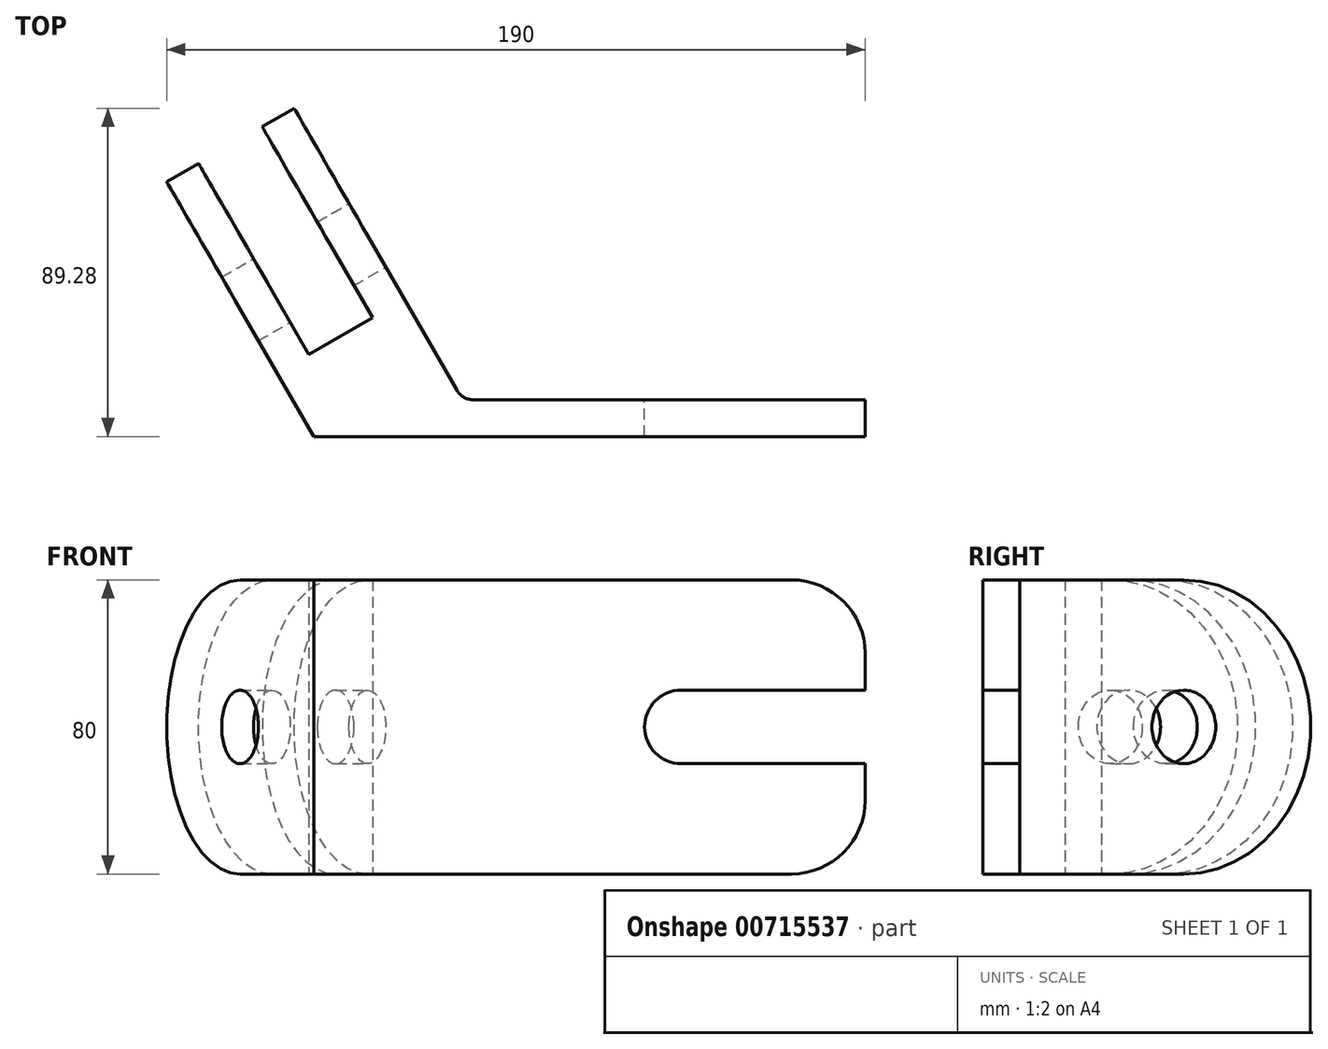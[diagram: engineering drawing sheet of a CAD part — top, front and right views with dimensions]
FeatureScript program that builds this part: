
annotation { "Feature Type Name" : "Feature", "Feature Type Description" : "" }
export const myFeature = defineFeature(function(context is Context, id is Id, definition is map)
    precondition{}
    {
        {
            var Q0;
            Q0=qCreatedBy(makeId("Top.planeOp"),FACE);
            var sketch = newSketch(context, id + "F0", { "sketchPlane" : qUnion([Q0])});
            skPoint(sketch, "E0.middle", {"position": v(0, 0) * mm});
            skLineSegment(sketch, "E1", {"start": v(0, 0) * mm, "end": v(150, 0) * mm});
            skLineSegment(sketch, "E2", {"start": v(150, 0) * mm, "end": v(150, 10) * mm});
            skLineSegment(sketch, "E3", {"start": v(0, 0) * mm, "end": v(-40, 69.28) * mm});
            skLineSegment(sketch, "E4", {"start": v(-40, 69.28) * mm, "end": v(-5.36, 89.28) * mm});
            skLineSegment(sketch, "E5", {"start": v(-5.36, 89.28) * mm, "end": v(40.41, 10) * mm});
            skLineSegment(sketch, "E6", {"start": v(150, 10) * mm, "end": v(40.41, 10) * mm});
            skLineSegment(sketch, "E7", {"start": v(-40, 69.28) * mm, "end": v(-31.34, 74.28) * mm});
            skLineSegment(sketch, "E8", {"start": v(-31.34, 74.28) * mm, "end": v(-1.34, 22.32) * mm});
            skLineSegment(sketch, "E9", {"start": v(-1.34, 22.32) * mm, "end": v(15.98, 32.32) * mm});
            skLineSegment(sketch, "E10", {"start": v(15.98, 32.32) * mm, "end": v(-14.02, 84.28) * mm});
            skSolve(sketch);
        }
        {
            var Q0;
            Q0=makeQuery(id+"F0.imprint","IMPRINT",FACE,{"disambiguationData":[TD([[makeQuery(id+"F0.imprint","IMPRINT",EDGE,{"derivedFrom":sQuery(id+"F0.wireOp",EDGE,"E1")}),1.0]])]});
            extrude(context, id + "F1", {"entities" : qUnion([Q0]), "depth" : 80 * mm, "offsetDistance" : 25 * mm});
        }
        {
            var Q0;
            Q0=makeQuery(id+"F1.opExtrude","SWEPT_FACE",FACE,{"disambiguationData":[OSD([sQuery(id+"F0.wireOp",EDGE,"E6")])]});
            var sketch = newSketch(context, id + "F2", { "sketchPlane" : qUnion([Q0])});
            skLineSegment(sketch, "E11", {"start": v(-150, 40) * mm, "end": v(-40.41, 40) * mm});
            skLineSegment(sketch, "E12.bottom", {"start": v(-210, 50) * mm, "end": v(-100, 50) * mm});
            skLineSegment(sketch, "E12.top", {"start": v(-210, 30) * mm, "end": v(-100, 30) * mm});
            skLineSegment(sketch, "E12.left", {"start": v(-210, 50) * mm, "end": v(-210, 30) * mm});
            skLineSegment(sketch, "E12.right", {"start": v(-90, 40) * mm, "end": v(-90, 40) * mm});
            skPoint(sketch, "E12.middle", {"position": v(-150, 40) * mm});
            skPoint(sketch, "E13.visualSharp", {"position": v(-90, 30) * mm});
            skArc(sketch, "E13.filletArc", {"start": v(-100, 30) * mm, "mid": v(-92.93, 32.93) * mm, "end": v(-90, 40) * mm});
            skPoint(sketch, "E14.visualSharp", {"position": v(-90, 50) * mm});
            skArc(sketch, "E14.filletArc", {"start": v(-90, 40) * mm, "mid": v(-92.93, 47.07) * mm, "end": v(-100, 50) * mm});
            skSolve(sketch);
        }
        {
            var Q0;
            {var subQ3=sQuery(id+"F2.wireOp",EDGE,"E13.filletArc");Q0=makeQuery(id+"F2.imprint","IMPRINT",FACE,{"disambiguationData":[TD([[makeQuery(id+"F2.imprint","IMPRINT",EDGE,{"derivedFrom":subQ3}),1.0]])]});}
            var Q1;
            {var subQ3=sQuery(id+"F2.wireOp",EDGE,"E14.filletArc");Q1=makeQuery(id+"F2.imprint","IMPRINT",FACE,{"disambiguationData":[TD([[makeQuery(id+"F2.imprint","IMPRINT",EDGE,{"derivedFrom":subQ3}),1.0]])]});}
            extrude(context, id + "F3", {"entities" : qUnion([Q0, Q1]), "operationType" : NewBodyOperationType.REMOVE, "oppositeDirection" : true, "depth" : 36 * mm, "offsetDistance" : 25 * mm});
        }
        {
            var Q0;
            Q0=makeQuery(id+"F1.opExtrude","CAP_EDGE",EDGE,{"disambiguationData":[OSD([sQuery(id+"F0.wireOp",EDGE,"E2")])],"isStart":false});
            var Q1;
            Q1=makeQuery(id+"F1.opExtrude","CAP_EDGE",EDGE,{"disambiguationData":[OSD([sQuery(id+"F0.wireOp",EDGE,"E2")])],"isStart":true});
            fillet(context, id + "F4", {"entities" : qUnion([Q0, Q1]), "radius" : 20 * mm, "tangentPropagation" : true, "allowEdgeOverflow" : false});
        }
        {
            var Q0;
            Q0=makeQuery(id+"F1.opExtrude","SWEPT_EDGE",EDGE,{"disambiguationData":[OSD([sQuery(id+"F0.wireOp",EDGE,"E5"),sQuery(id+"F0.wireOp",EDGE,"E6")])]});
            fillet(context, id + "F5", {"entities" : qUnion([Q0]), "radius" : 5 * mm, "tangentPropagation" : true, "allowEdgeOverflow" : false});
        }
        {
            var Q0;
            Q0=makeQuery(id+"F1.opExtrude","CAP_EDGE",EDGE,{"disambiguationData":[OSD([sQuery(id+"F0.wireOp",EDGE,"E4")])],"isStart":true});
            var Q1;
            Q1=makeQuery(id+"F1.opExtrude","CAP_EDGE",EDGE,{"disambiguationData":[OSD([sQuery(id+"F0.wireOp",EDGE,"E4")])],"isStart":false});
            var Q2;
            Q2=makeQuery(id+"F1.opExtrude","CAP_EDGE",EDGE,{"disambiguationData":[OSD([sQuery(id+"F0.wireOp",EDGE,"E7")])],"isStart":false});
            var Q3;
            Q3=makeQuery(id+"F1.opExtrude","CAP_EDGE",EDGE,{"disambiguationData":[OSD([sQuery(id+"F0.wireOp",EDGE,"E7")])],"isStart":true});
            fillet(context, id + "F6", {"entities" : qUnion([Q0, Q1, Q2, Q3]), "radius" : 40 * mm, "tangentPropagation" : true, "allowEdgeOverflow" : false});
        }
        {
            var Q0;
            Q0=makeQuery(id+"F1.opExtrude","SWEPT_FACE",FACE,{"disambiguationData":[OSD([sQuery(id+"F0.wireOp",EDGE,"E5")])]});
            var sketch = newSketch(context, id + "F7", { "sketchPlane" : qUnion([Q0])});
            skLineSegment(sketch, "E15", {"start": v(40, 80) * mm, "end": v(40, 50) * mm});
            skLineSegment(sketch, "E16", {"start": v(-8.66, 40) * mm, "end": v(30.07, 40) * mm});
            skCircle(sketch, "E17", {"center": v(40.07, 40) * mm, "radius": 10 * mm});
            skLineSegment(sketch, "E18.trimOffspring", {"start": v(40, 40) * mm, "end": v(40.07, 40) * mm});
            skLineSegment(sketch, "E19.trimOffspring", {"start": v(40, 30) * mm, "end": v(40, 0) * mm});
            skLineSegment(sketch, "E20.trimOffspring", {"start": v(50.07, 40) * mm, "end": v(80, 40) * mm});
            skSolve(sketch);
        }
        {
            var Q0;
            {var subQ0=sQuery(id+"F7.wireOp",EDGE,"E17");var subQ1=makeQuery(id+"F7.imprint","INTERSECT",VERTEX,{"derivedFrom":[sQuery(id+"F7.wireOp",EDGE,"E15"),subQ0]});Q0=makeQuery(id+"F7.imprint","IMPRINT",FACE,{"disambiguationData":[TD([[makeQuery(id+"F7.imprint","IMPRINT",EDGE,{"disambiguationData":[TD([[subQ1,1.0]])],"derivedFrom":subQ0}),1.0]])]});}
            extrude(context, id + "F8", {"entities" : qUnion([Q0]), "operationType" : NewBodyOperationType.REMOVE, "oppositeDirection" : true, "depth" : 85 * mm, "offsetDistance" : 25 * mm});
        }
    });
